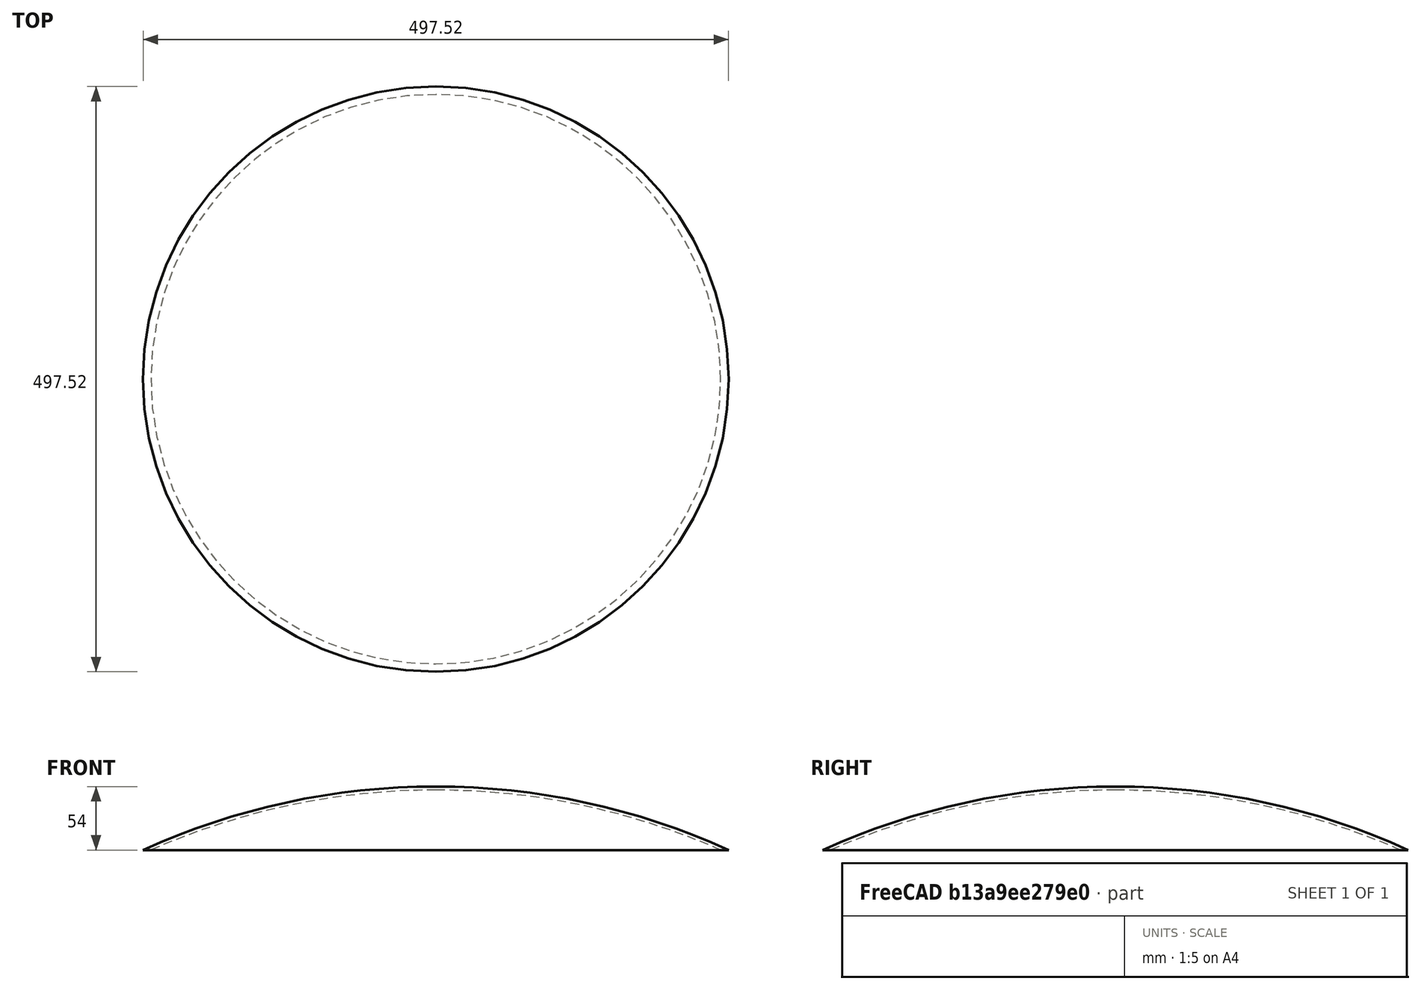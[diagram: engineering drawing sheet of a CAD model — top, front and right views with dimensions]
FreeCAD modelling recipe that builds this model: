
FCSTD DOCUMENT  (FreeCAD 0.18R16110 (Git))
Label: spoon_v1
License: All rights reserved
LicenseURL: http://en.wikipedia.org/wiki/All_rights_reserved
objects: Part::Cut×3, Part::Sphere×2, Part::Cylinder×2, PartDesign::Body×1
note: 8 computed .brp shape members not serialized (recipe doc carries the construction recipe); baked Part::Feature solids carry a one-line shape summary decoded from their .brp

FEATURE [PartDesign::Body] Body
  Origin = -> Origin
FEATURE [Part::Sphere] Sphere
  Angle1 = -90
  Angle2 = 90
  Angle3 = 360
  AttacherType = Attacher::AttachEngine3D
  Radius = 600
FEATURE [Part::Cylinder] Cylinder
  Angle = 360
  AttacherType = Attacher::AttachEngine3D
  Height = 1200
  Placement = pos=(0,0,-654) rot=(0,0,1;0rad)
  Radius = 600
FEATURE [Part::Cut] Cut
  Base = -> Sphere
  Tool = -> Cylinder
FEATURE [Part::Cylinder] Cylinder001
  Angle = 360
  AttacherType = Attacher::AttachEngine3D
  Height = 1200
  Placement = pos=(0,0,-654) rot=(0,0,1;0rad)
  Radius = 600
FEATURE [Part::Sphere] Sphere001
  Angle1 = -90
  Angle2 = 90
  Angle3 = 360
  AttacherType = Attacher::AttachEngine3D
  Radius = 600
FEATURE [Part::Cut] Cut001
  Base = -> Sphere001
  Placement = pos=(0,0,-3) rot=(0,0,1;0rad)
  Tool = -> Cylinder001
FEATURE [Part::Cut] Cut002
  Base = -> Cut
  Tool = -> Cut001
